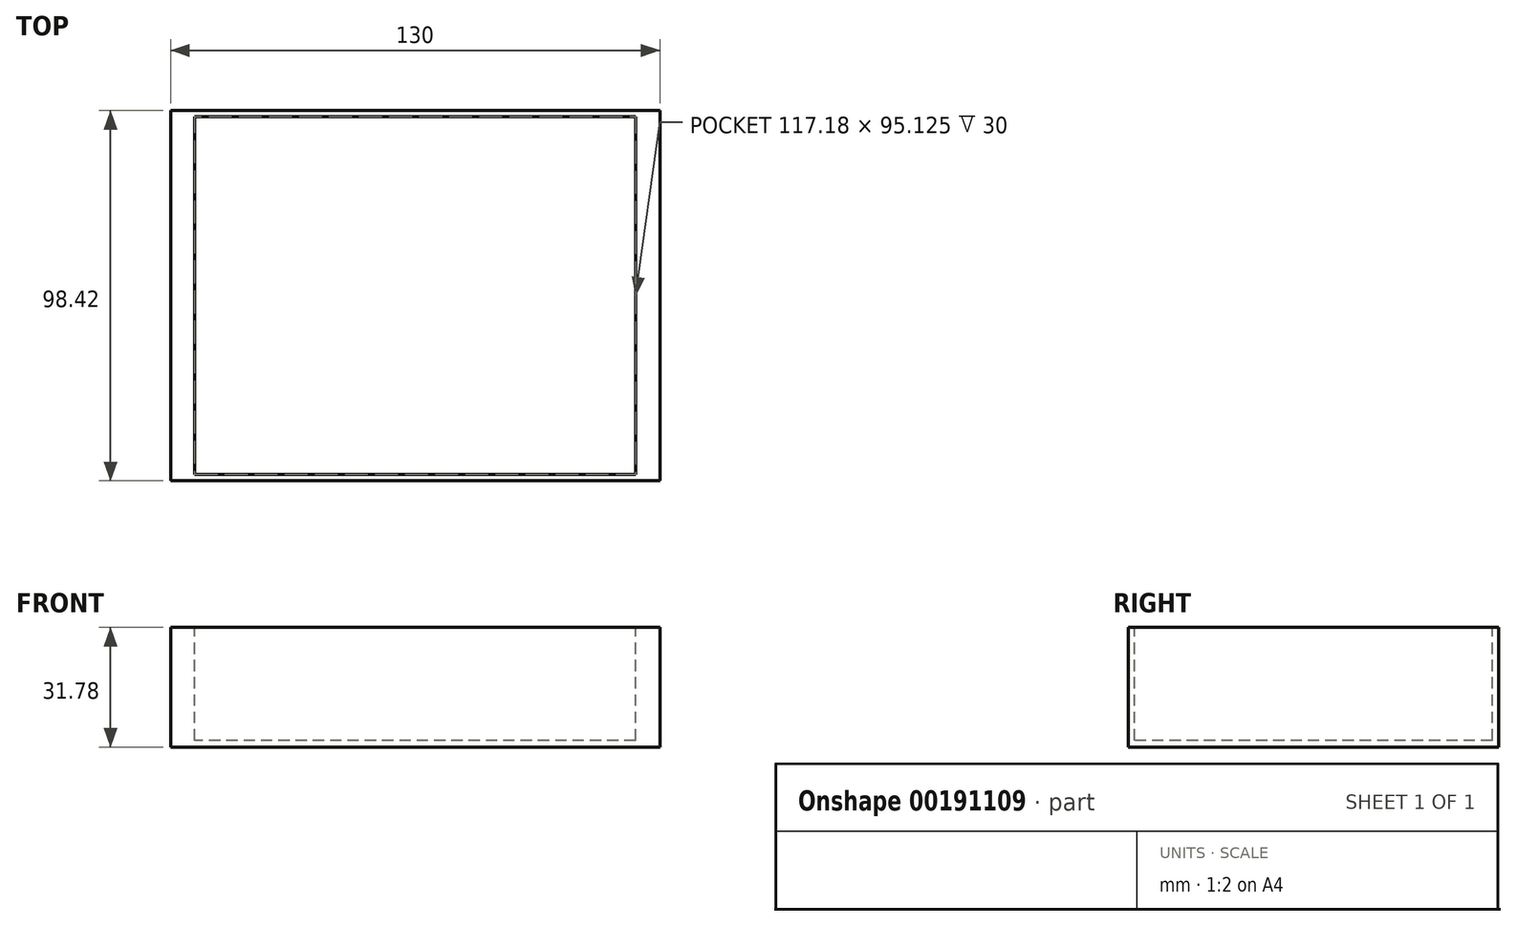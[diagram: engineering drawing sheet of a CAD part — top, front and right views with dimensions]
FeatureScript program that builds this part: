
annotation { "Feature Type Name" : "Feature", "Feature Type Description" : "" }
export const myFeature = defineFeature(function(context is Context, id is Id, definition is map)
    precondition{}
    {
        {
            var Q0;
            Q0=qCreatedBy(makeId("Top.planeOp"),FACE);
            var sketch = newSketch(context, id + "F0", { "sketchPlane" : qUnion([Q0])});
            skLineSegment(sketch, "E0.bottom", {"start": v(65, -49.21) * mm, "end": v(-65, -49.21) * mm});
            skLineSegment(sketch, "E0.top", {"start": v(65, 49.21) * mm, "end": v(-65, 49.21) * mm});
            skLineSegment(sketch, "E0.left", {"start": v(65, -49.21) * mm, "end": v(65, 49.21) * mm});
            skLineSegment(sketch, "E0.right", {"start": v(-65, -49.21) * mm, "end": v(-65, 49.21) * mm});
            skPoint(sketch, "E0.middle", {"position": v(0, 0) * mm});
            skSolve(sketch);
        }
        {
            var Q0;
            Q0=makeQuery(id+"F0.imprint","IMPRINT",FACE,{"disambiguationData":[TD([[makeQuery(id+"F0.imprint","IMPRINT",EDGE,{"derivedFrom":sQuery(id+"F0.wireOp",EDGE,"E0.bottom")}),-1.0]])]});
            extrude(context, id + "F1", {"entities" : qUnion([Q0]), "depth" : 31.78 * mm});
        }
        {
            var Q0;
            Q0=makeQuery(id+"F1.opExtrude","CAP_FACE",FACE,{"disambiguationData":[OSD([sQuery(id+"F0.wireOp",EDGE,"E0.bottom"),sQuery(id+"F0.wireOp",EDGE,"E0.top"),sQuery(id+"F0.wireOp",EDGE,"E0.left"),sQuery(id+"F0.wireOp",EDGE,"E0.right")])],"isStart":false});
            var sketch = newSketch(context, id + "F2", { "sketchPlane" : qUnion([Q0])});
            skLineSegment(sketch, "E1.bottom", {"start": v(58.6, 47.56) * mm, "end": v(-58.6, 47.56) * mm});
            skLineSegment(sketch, "E1.top", {"start": v(58.6, -47.56) * mm, "end": v(-58.6, -47.56) * mm});
            skLineSegment(sketch, "E1.left", {"start": v(58.6, 47.56) * mm, "end": v(58.6, -47.56) * mm});
            skLineSegment(sketch, "E1.right", {"start": v(-58.6, 47.56) * mm, "end": v(-58.6, -47.56) * mm});
            skPoint(sketch, "E1.middle", {"position": v(0, 0) * mm});
            skSolve(sketch);
        }
        {
            var Q0;
            Q0=qSketchRegion(id+"F2",true);
            extrude(context, id + "F3", {"entities" : qUnion([Q0]), "operationType" : NewBodyOperationType.REMOVE, "oppositeDirection" : true, "depth" : 30 * mm});
        }
    });
